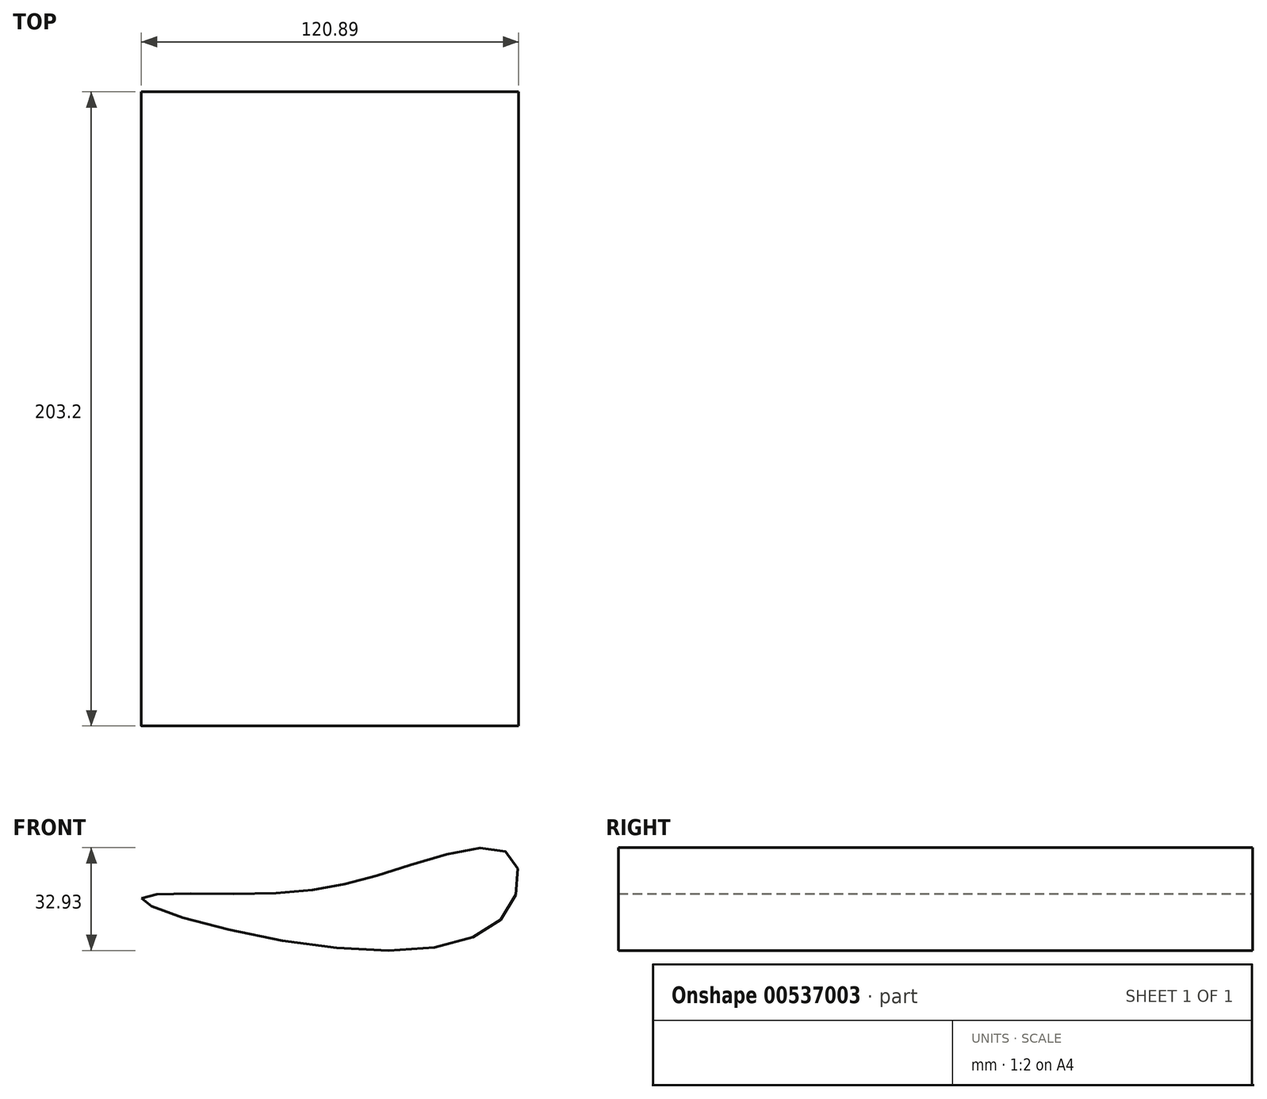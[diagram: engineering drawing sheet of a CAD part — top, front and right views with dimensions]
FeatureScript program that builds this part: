
annotation { "Feature Type Name" : "Feature", "Feature Type Description" : "" }
export const myFeature = defineFeature(function(context is Context, id is Id, definition is map)
    precondition{}
    {
        {
            var Q0;
            Q0=qCreatedBy(makeId("Front.planeOp"),FACE);
            var sketch = newSketch(context, id + "F0", { "sketchPlane" : qUnion([Q0])});
            skFitSpline(sketch, "E0", {"points": [v(-50.31, -11.3) * mm, v(0, -25.7) * mm, v(65.6, -17.31) * mm, v(67.42, 2.92) * mm, v(31.88, -2) * mm, v(-10.4, -9.84) * mm, v(-50.31, -11.3) * mm]});
            skSolve(sketch);
        }
        {
            var Q0;
            Q0=makeQuery(id+"F0.imprint","IMPRINT",FACE,{"disambiguationData":[TD([[makeQuery(id+"F0.imprint","IMPRINT",EDGE,{"derivedFrom":sQuery(id+"F0.wireOp",EDGE,"E0")}),1.0]])]});
            extrude(context, id + "F1", {"entities" : qUnion([Q0]), "depth" : 203.2 * mm, "offsetDistance" : 25.4 * mm});
        }
    });
